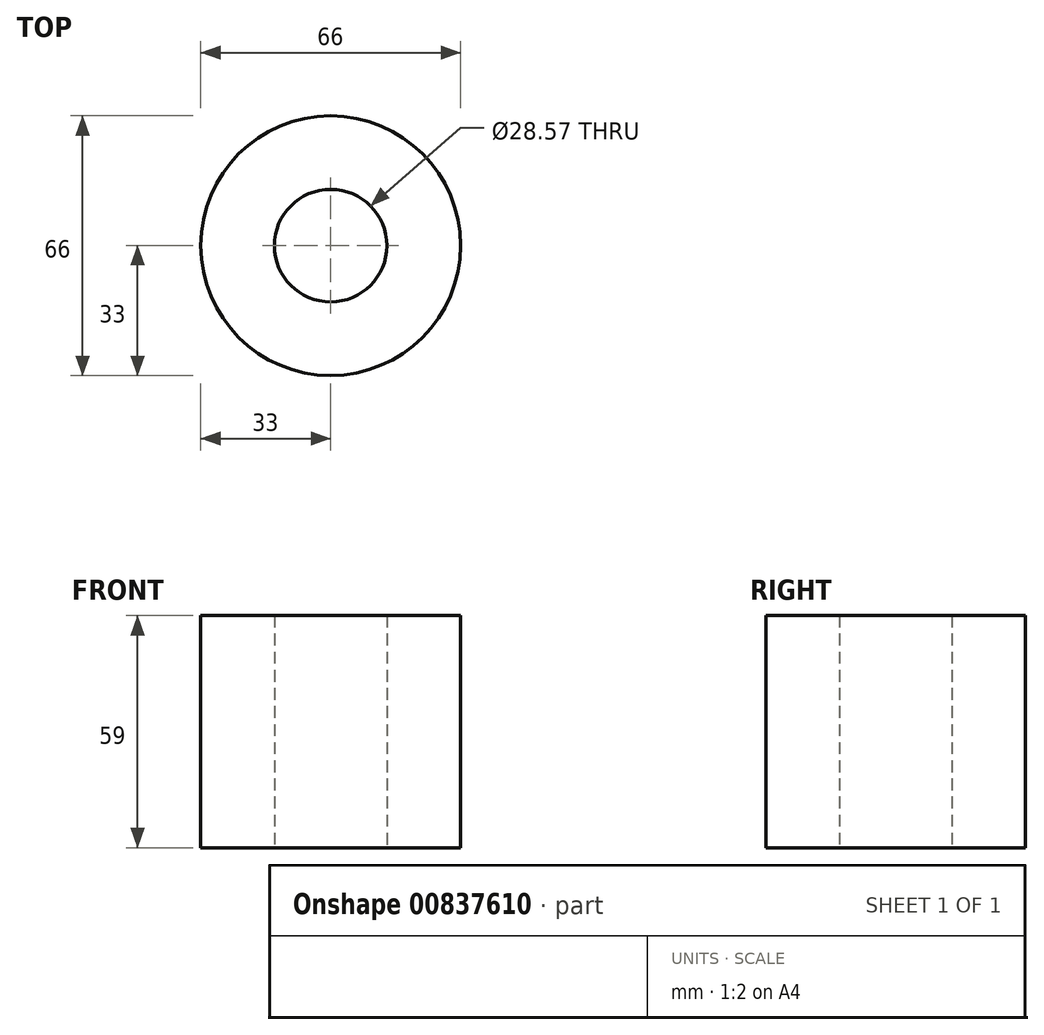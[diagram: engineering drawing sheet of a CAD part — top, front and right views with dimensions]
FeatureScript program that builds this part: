
annotation { "Feature Type Name" : "Feature", "Feature Type Description" : "" }
export const myFeature = defineFeature(function(context is Context, id is Id, definition is map)
    precondition{}
    {
        {
            var Q0;
            Q0=qCreatedBy(makeId("Top.planeOp"),FACE);
            var sketch = newSketch(context, id + "F0", { "sketchPlane" : qUnion([Q0])});
            skCircle(sketch, "E0", {"center": v(0, 0) * mm, "radius": 33 * mm});
            skCircle(sketch, "E1", {"center": v(0, 0) * mm, "radius": 14.29 * mm});
            skSolve(sketch);
        }
        {
            var Q0;
            Q0=makeQuery(id+"F0.imprint","IMPRINT",FACE,{"disambiguationData":[TD([[makeQuery(id+"F0.imprint","IMPRINT",EDGE,{"derivedFrom":sQuery(id+"F0.wireOp",EDGE,"E0")}),1.0]])]});
            extrude(context, id + "F1", {"entities" : qUnion([Q0]), "depth" : 59 * mm, "offsetDistance" : 25.4 * mm});
        }
    });
